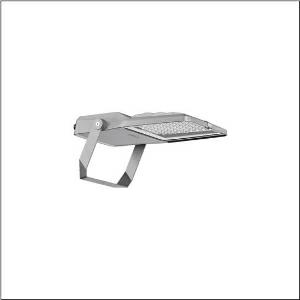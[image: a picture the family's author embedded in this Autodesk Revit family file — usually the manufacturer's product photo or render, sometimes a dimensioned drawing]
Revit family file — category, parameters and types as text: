
# Revit family: floodlight_fl_21_iq_mini___pl43_5xa7772d1a1a_00f7
name_source: partatom
category: Lighting Fixtures
units: mm (PartAtom-declared; Revit-internal decimal feet)

## family parameters
Cut with Voids When Loaded = No
Host = Face
Light Source = No
Part Type = Normal
Room Calculation Point = No
Round Connector Dimension = Use Diameter
Shared = No

## types (1)
- --- (1 x LED, 15140 lm, 143 W, 2200K)
    Apparent Load = 143 VA
    CIE Flux Codes = 27 78 99 100 100
    Color Rendering = 70
    Color Temperature = 2200K
    Default Elevation = 1800 mm
    Description = Floodlight FL 21 iQ mini, floodlight, primary light control with lens, of PMMA, primary optical cover: protective disc, of toughened safety glass, transparent, light distribution: PL43, light emission: direct distribution, installation type: surface-mounted, LED, High Power LED, rated luminous flux: 15.140lm, luminous efficacy: 106lm/W, light colour: 722, colour temperature: 2200K, control gear: iQ Street-Remote/DALI, control: Street-Remote, Auto-Match, Temp-Guard, Night-Set, Smart-Wire, Desk-Remote (wireless, voltage-free reading and setting of iQ features in the workshop via application-optimized NFC function/RFID function), optimised constant luminous flux control (CLO 2.0), with terminal, 6-pole, mains connection: 220..240V, AC, 50/60Hz, start of lifetime: 143W, end of service life: 152W, reduction: 61W, luminaire housing, of diecast aluminium, powder-coated, Siteco® metallic grey (DB 702S), corrosivity category C5 mid according to DIN EN ISO 12944, suitable for swimming pools, chlorine-resistant, sealing non-destructively replaceable, mounting bracket, of steel, galvanised, powder-coated, Siteco® metallic grey (DB 702S), protection rating (complete): IP66, insulation class (complete): insulation class II (safety insulation), certification: CE, ENEC, VDE, protection symbol: D, impact resistance: IK08, permissible operating ambient temperature: -40..+40°C, permissible operating ambient temperature for outdoor applications: -40..+50°C, standard: DIN EN 12944, LABS conformity tested according to VDMA 24364:2018-05, packaging unit: 1 piece

Light Distribution: PL43
    Height = 70 mm
    Lamp = 1 x LED
    Lamp Light Flux = 15140 lm
    Lamp Power = 143 W
    Lamp count = 1
    Length = 485 mm
    Luminous efficacy = 106 lm/W
    Manufacturer = Siteco
    ModVariant = No
    Model = 5XA7772D1A1A
    Number of Poles = 1
    OnlyDefault = Yes
    Power Factor = 1
    Product Name = Floodlight FL 21 iQ mini | PL43
    Product group = floodlight | pylon annexe
    ProductGroupID = 6200
    Protection Class = Protection class II
    Protection Degree = IP 66
    RLX_Detail_Level = 1
    RLX_Emergency_Light_Flux = 0 lm
    RLX_Emergency_Type = 0
    RLX_Emergency_Type_DB = No
    RlxData = <blob elided: 96393 chars, md5=e36c8b29>
    Socket = socket
    Standby Power = 0 W
    System Light Flux = 15140 lm
    System Power = 143 W
    Type Comments = factory setting: luminous flux: 100 % | dim-lin: 254 | 730 mA
    Type Image = l_1006845.jpg
    URL = http://relux.com
    VarID = @adj_161716
    Voltage = 0 V
    Weight = 0.00 kg
    Width = 337 mm

## geometry (parser evidence)
native form markers: Blend x4, Sweep x11
no freeform markers — native parametric forms only
